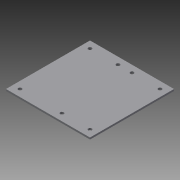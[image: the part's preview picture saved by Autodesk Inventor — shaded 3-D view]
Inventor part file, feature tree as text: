
AUTODESK INVENTOR PART (.ipt)
format: ipt  version: 2015 (Build 190159000, 159)  size: 96,768 bytes
history: native  units: in
note: dims shown in document units (in); Inventor stores cm internally (conversion verified against a paired STEP export)
features: sketch x3, hole x2, extrude x1
ambient origin geometry x8: Origin, YZ Plane, XZ Plane, XY Plane, X Axis, Y Axis, Z Axis, Center Point
bodies: Solid1 (feature_tree)
feature tree (6):
  extrude  "Extrusion1"  Depth=6.0in
  hole  "Hole1"  [1 undecoded]
  hole  "Hole2"  [1 undecoded]
  sketch  "Sketch1"  dims[d0=6.0in d1=6.0in]
  sketch  "Sketch2"  dims[d2=0.125in d3=0.0in d4=0.5in]
  sketch  "Sketch3"  dims[d5=0.5in d6=0.5in d7=0.5in d8=0.5in d9=0.5in d10=0.5in d11=2.5in d12=0.5in d13=0.5in d14=0.5in d15=2.5in d16=0.25in d17=0.75in d18=0.375in d19=0.25in d20=0.5635in d21=1.0in d22=0.8108in d23=0.5in d24=2.0in d25=0.25in d26=0.75in d27=0.375in d28=0.25in d29=0.5635in d30=1.0in d31=0.8108in]
note: 2 required parameter values undecoded (feature->parameter linkage not recoverable at this tier; creation-order binding heuristic only, values carry confidence <= 0.55)
